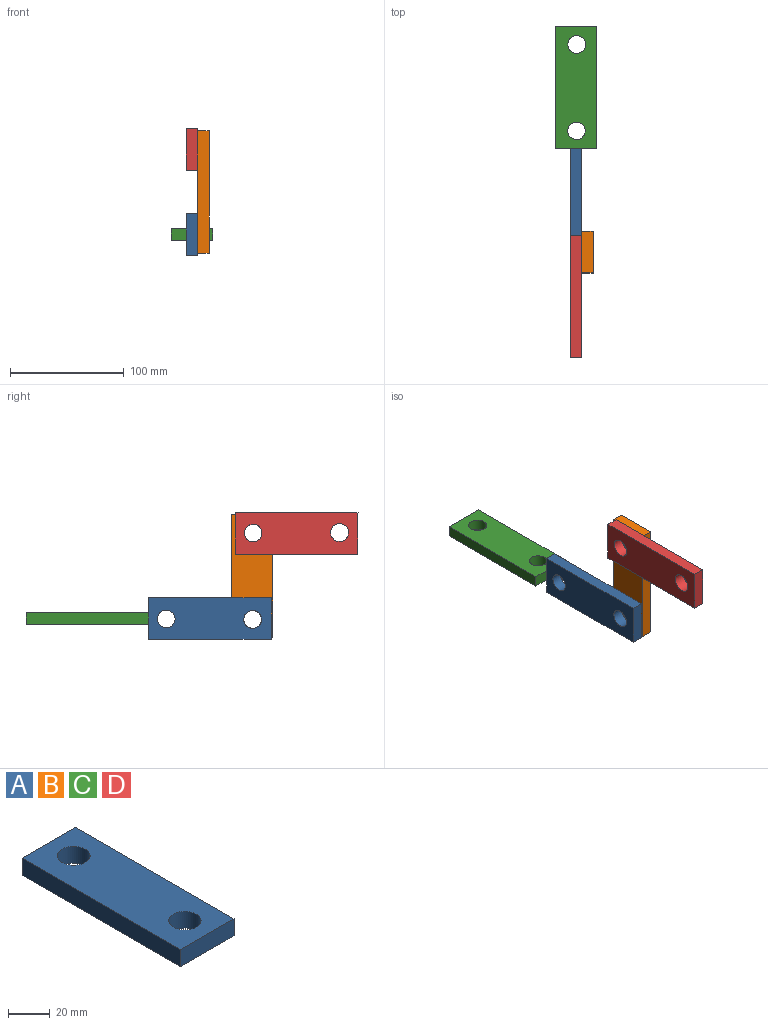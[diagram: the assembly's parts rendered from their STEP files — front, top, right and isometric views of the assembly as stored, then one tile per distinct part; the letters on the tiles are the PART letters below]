
ASSEMBLY  parts=4 mates=3
PART A: 8 faces, bbox 36.3x107.6x10 mm
  f0: plane 36.26x10mm, normal (0,1,0), area 362.6mm2, adj f1,f5,f6,f7
  f1: plane 107.6x10mm, normal (-1,0,0), area 1076mm2, adj f0,f2,f6,f7
  f2: plane 36.26x10mm, normal (0,-1,0), area 362.6mm2, adj f1,f5,f6,f7
  f3: cylinder r=7.85mm len=15.7mm, axis (0,0,-1), area 493.1mm2, adj f6,f7
  f4: cylinder r=7.73mm len=15.45mm, axis (0,0,-1), area 485.4mm2, adj f6,f7
  f5: plane 107.6x10mm, normal (1,0,0), area 1076mm2, adj f0,f2,f6,f7
  f6: plane 107.6x36.26mm, normal (0,0,1), area 3520.6mm2, adj f0,f1,f2,f3,f4,f5
  f7: plane 107.6x36.26mm, normal (0,0,-1), area 3520.6mm2, adj f0,f1,f2,f3,f4,f5
PART B: same geometry as A
PART C: same geometry as A
PART D: same geometry as A
PLACE A rot(axis=(-0.71,0,0.71),180deg) t=(-5.33,-57.16,-95.44)mm
PLACE B rot(axis=(0.58,-0.58,-0.58),120deg) t=(4.67,-96.18,-36.72)mm
PLACE C t=(1.19,69.95,-88.91)mm
PLACE D rot(axis=(-0.71,0,-0.71),180deg) t=(-15.33,-133.43,2.3)mm
MATE fastened A.f2 <-> C.f2  axis (0,1,0) through (-10.33,6.39,-83.91)mm
MATE revolute B.f4 <-> A.f3  axis (-1,0,0) through (-5.33,-85.05,-84.7)mm
MATE slider D.f4 <-> B.f3  axis (-1,0,0) through (-15.33,-85.44,-8.83)mm
